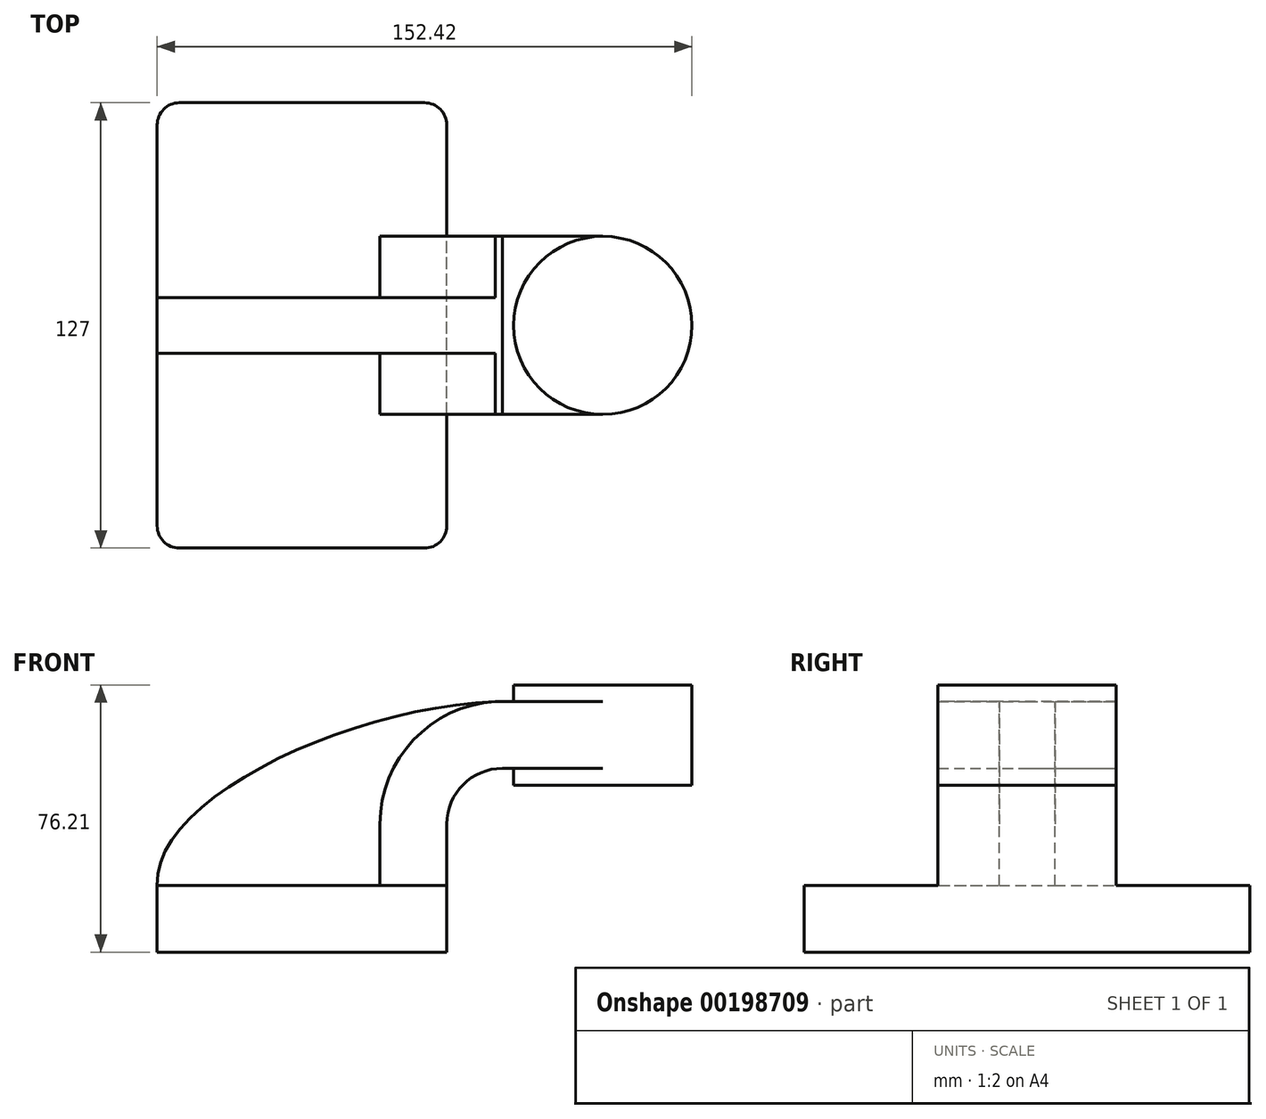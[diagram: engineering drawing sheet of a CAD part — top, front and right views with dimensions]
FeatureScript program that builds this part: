
annotation { "Feature Type Name" : "Feature", "Feature Type Description" : "" }
export const myFeature = defineFeature(function(context is Context, id is Id, definition is map)
    precondition{}
    {
        {
            var Q0;
            Q0=qCreatedBy(makeId("Front.planeOp"),FACE);
            var sketch = newSketch(context, id + "F0", { "sketchPlane" : qUnion([Q0])});
            skLineSegment(sketch, "E0.bottom", {"start": v(41.27, 9.53) * mm, "end": v(-41.28, 9.53) * mm});
            skLineSegment(sketch, "E0.top", {"start": v(41.28, -9.52) * mm, "end": v(-41.27, -9.52) * mm});
            skLineSegment(sketch, "E0.left", {"start": v(41.28, 9.53) * mm, "end": v(41.28, -9.52) * mm});
            skLineSegment(sketch, "E0.right", {"start": v(-41.28, 9.53) * mm, "end": v(-41.27, -9.52) * mm});
            skPoint(sketch, "E0.middle", {"position": v(0, 0) * mm});
            skLineSegment(sketch, "E1.bottom", {"start": v(60.33, 66.68) * mm, "end": v(111.12, 66.68) * mm});
            skLineSegment(sketch, "E1.top", {"start": v(60.33, 38.1) * mm, "end": v(111.12, 38.1) * mm});
            skLineSegment(sketch, "E1.left", {"start": v(60.33, 66.67) * mm, "end": v(60.33, 38.1) * mm});
            skLineSegment(sketch, "E1.right", {"start": v(111.13, 66.68) * mm, "end": v(111.13, 38.1) * mm});
            skLineSegment(sketch, "E2", {"start": v(41.27, 9.53) * mm, "end": v(41.27, 27) * mm});
            skLineSegment(sketch, "E3", {"start": v(85.73, 38.1) * mm, "end": v(85.73, 66.68) * mm});
            skLineSegment(sketch, "E4", {"start": v(85.73, 42.88) * mm, "end": v(57.15, 42.88) * mm});
            skArc(sketch, "E5.filletArc", {"start": v(57.15, 42.88) * mm, "mid": v(45.92, 38.23) * mm, "end": v(41.28, 27) * mm});
            skLineSegment(sketch, "E6.0", {"start": v(22.23, 9.53) * mm, "end": v(22.23, 27) * mm});
            skArc(sketch, "E6.1", {"start": v(57.15, 61.93) * mm, "mid": v(32.45, 51.7) * mm, "end": v(22.23, 27) * mm});
            skLineSegment(sketch, "E6.2", {"start": v(85.73, 61.93) * mm, "end": v(57.15, 61.93) * mm});
            skFitSpline(sketch, "E7", {"points": [v(-41.28, 9.53) * mm, v(57.15, 61.93) * mm], "startDerivative": vector(-3.42, 75.34) * mm, "endDerivative": vector(127.37, 2.52) * mm});
            skSolve(sketch);
        }
        {
            var Q0;
            Q0=makeQuery(id+"F0.imprint","IMPRINT",FACE,{"disambiguationData":[TD([[makeQuery(id+"F0.imprint","IMPRINT",EDGE,{"derivedFrom":sQuery(id+"F0.wireOp",EDGE,"E0.top")}),-1.0]])]});
            extrude(context, id + "F1", {"entities" : qUnion([Q0]), "endBound" : BoundingType.SYMMETRIC, "depth" : 127 * mm});
        }
        {
            var Q0;
            {var subQ0=sQuery(id+"F0.wireOp",EDGE,"E2");Q0=makeQuery(id+"F0.imprint","IMPRINT",FACE,{"disambiguationData":[TD([[makeQuery(id+"F0.imprint","IMPRINT",EDGE,{"derivedFrom":subQ0}),1.0]])]});}
            var Q1;
            {var subQ0=sQuery(id+"F0.wireOp",EDGE,"E6.2");var subQ1=sQuery(id+"F0.wireOp",EDGE,"E1.left");var subQ2=makeQuery(id+"F0.imprint","INTERSECT",VERTEX,{"derivedFrom":[subQ1,subQ0]});Q1=makeQuery(id+"F0.imprint","IMPRINT",FACE,{"disambiguationData":[TD([[makeQuery(id+"F0.imprint","IMPRINT",EDGE,{"disambiguationData":[TD([[subQ2,-1.0]])],"derivedFrom":subQ1}),1.0]])]});}
            extrude(context, id + "F2", {"entities" : qUnion([Q0, Q1]), "operationType" : NewBodyOperationType.ADD, "endBound" : BoundingType.SYMMETRIC, "depth" : 50.8 * mm});
        }
        {
            var Q0;
            {var subQ3=sQuery(id+"F0.wireOp",EDGE,"E6.0");Q0=makeQuery(id+"F0.imprint","IMPRINT",FACE,{"disambiguationData":[TD([[makeQuery(id+"F0.imprint","IMPRINT",EDGE,{"derivedFrom":subQ3}),1.0]])]});}
            extrude(context, id + "F3", {"entities" : qUnion([Q0]), "operationType" : NewBodyOperationType.ADD, "endBound" : BoundingType.SYMMETRIC, "depth" : 15.88 * mm});
        }
        {
            var Q0;
            {var subQ4=sQuery(id+"F0.wireOp",EDGE,"E1.right");Q0=makeQuery(id+"F0.imprint","IMPRINT",FACE,{"disambiguationData":[TD([[makeQuery(id+"F0.imprint","IMPRINT",EDGE,{"derivedFrom":subQ4}),-1.0]])]});}
            var Q1;
            Q1=sQuery(id+"F0.wireOp",EDGE,"E3");
            revolve(context, id + "F4", {"operationType" : NewBodyOperationType.ADD, "entities" : qUnion([Q0]), "axis" : qUnion([Q1]), "revolveType" : RevolveType.FULL});
        }
        {
            var Q0;
            Q0=makeQuery(id+"F1.opExtrude","CAP_EDGE",EDGE,{"disambiguationData":[OSD([sQuery(id+"F0.wireOp",EDGE,"E0.right")])],"isStart":false});
            var Q1;
            Q1=makeQuery(id+"F1.opExtrude","CAP_EDGE",EDGE,{"disambiguationData":[OSD([sQuery(id+"F0.wireOp",EDGE,"E0.left")])],"isStart":false});
            var Q2;
            Q2=makeQuery(id+"F1.opExtrude","CAP_EDGE",EDGE,{"disambiguationData":[OSD([sQuery(id+"F0.wireOp",EDGE,"E0.left")])],"isStart":true});
            var Q3;
            Q3=makeQuery(id+"F1.opExtrude","CAP_EDGE",EDGE,{"disambiguationData":[OSD([sQuery(id+"F0.wireOp",EDGE,"E0.right")])],"isStart":true});
            fillet(context, id + "F5", {"entities" : qUnion([Q0, Q1, Q2, Q3]), "radius" : 6.35 * mm, "tangentPropagation" : true, "allowEdgeOverflow" : false});
        }
    });
